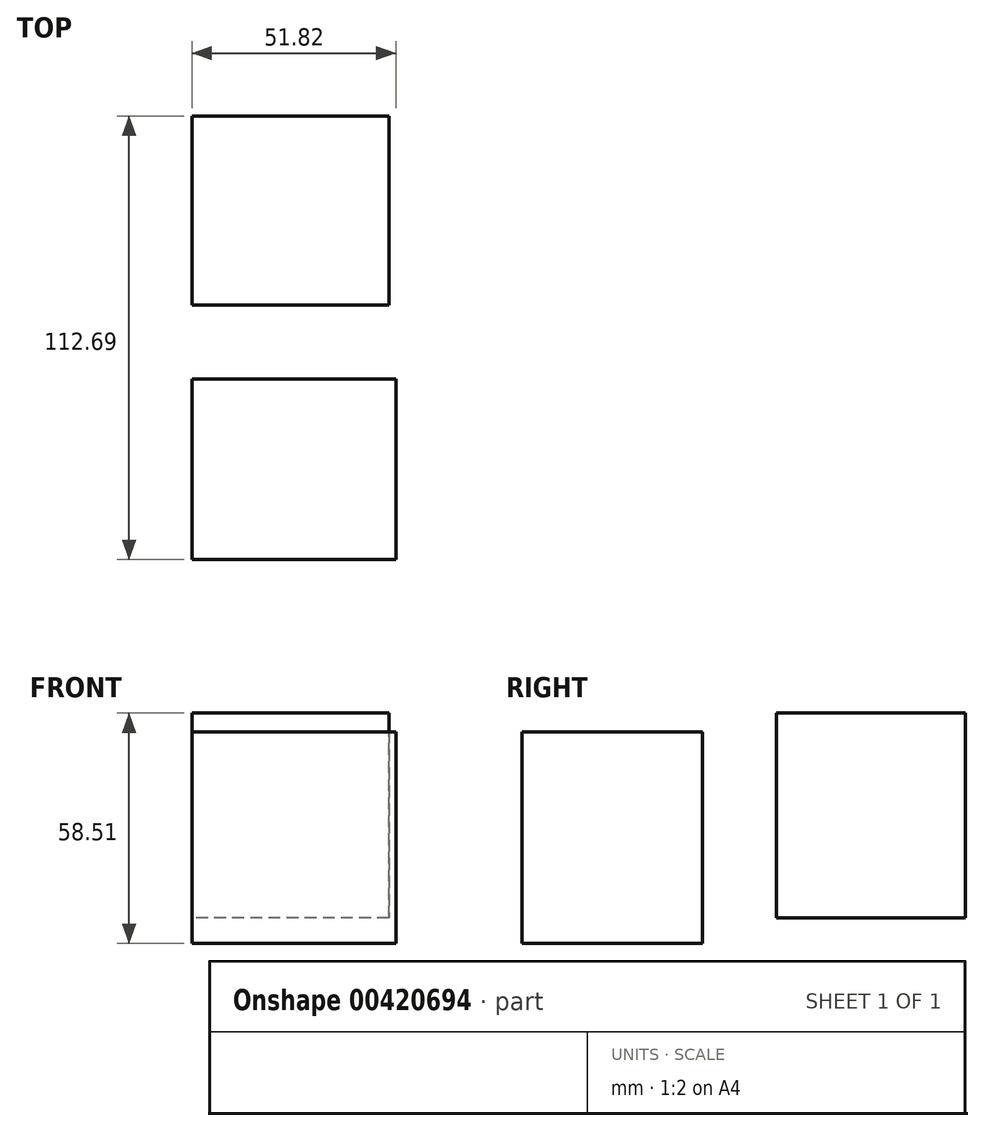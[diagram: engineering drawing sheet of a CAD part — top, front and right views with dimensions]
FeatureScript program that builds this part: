
annotation { "Feature Type Name" : "Feature", "Feature Type Description" : "" }
export const myFeature = defineFeature(function(context is Context, id is Id, definition is map)
    precondition{}
    {
        {
            var Q0;
            Q0=qCreatedBy(makeId("Right.planeOp"),FACE);
            var sketch = newSketch(context, id + "F0", { "sketchPlane" : qUnion([Q0])});
            skLineSegment(sketch, "E0", {"start": v(112.7, 58.51) * mm, "end": v(112.7, 6.5) * mm});
            skLineSegment(sketch, "E1", {"start": v(112.7, 6.5) * mm, "end": v(64.62, 6.5) * mm});
            skLineSegment(sketch, "E2", {"start": v(112.7, 58.51) * mm, "end": v(64.62, 58.51) * mm});
            skLineSegment(sketch, "E3", {"start": v(64.62, 6.5) * mm, "end": v(64.62, 58.51) * mm});
            skSolve(sketch);
        }
        {
            var Q0;
            Q0=makeQuery(id+"F0.imprint","IMPRINT",FACE,{"disambiguationData":[TD([[makeQuery(id+"F0.imprint","IMPRINT",EDGE,{"derivedFrom":sQuery(id+"F0.wireOp",EDGE,"E0")}),-1.0]])]});
            extrude(context, id + "F1", {"entities" : qUnion([Q0]), "depth" : 50.04 * mm});
        }
        {
            var Q0;
            Q0=qCreatedBy(makeId("Right.planeOp"),FACE);
            var sketch = newSketch(context, id + "F2", { "sketchPlane" : qUnion([Q0])});
            skLineSegment(sketch, "E4", {"start": v(45.92, 53.77) * mm, "end": v(45.92, 0) * mm});
            skLineSegment(sketch, "E5", {"start": v(45.92, 0) * mm, "end": v(0, 0) * mm});
            skLineSegment(sketch, "E6", {"start": v(45.92, 53.77) * mm, "end": v(0, 53.77) * mm});
            skLineSegment(sketch, "E7", {"start": v(0, 53.77) * mm, "end": v(0, 0) * mm});
            skSolve(sketch);
        }
        {
            var Q0;
            Q0=makeQuery(id+"F2.imprint","IMPRINT",FACE,{"disambiguationData":[TD([[makeQuery(id+"F2.imprint","IMPRINT",EDGE,{"derivedFrom":sQuery(id+"F2.wireOp",EDGE,"E4")}),-1.0]])]});
            extrude(context, id + "F3", {"entities" : qUnion([Q0]), "depth" : 51.82 * mm});
        }
    });
